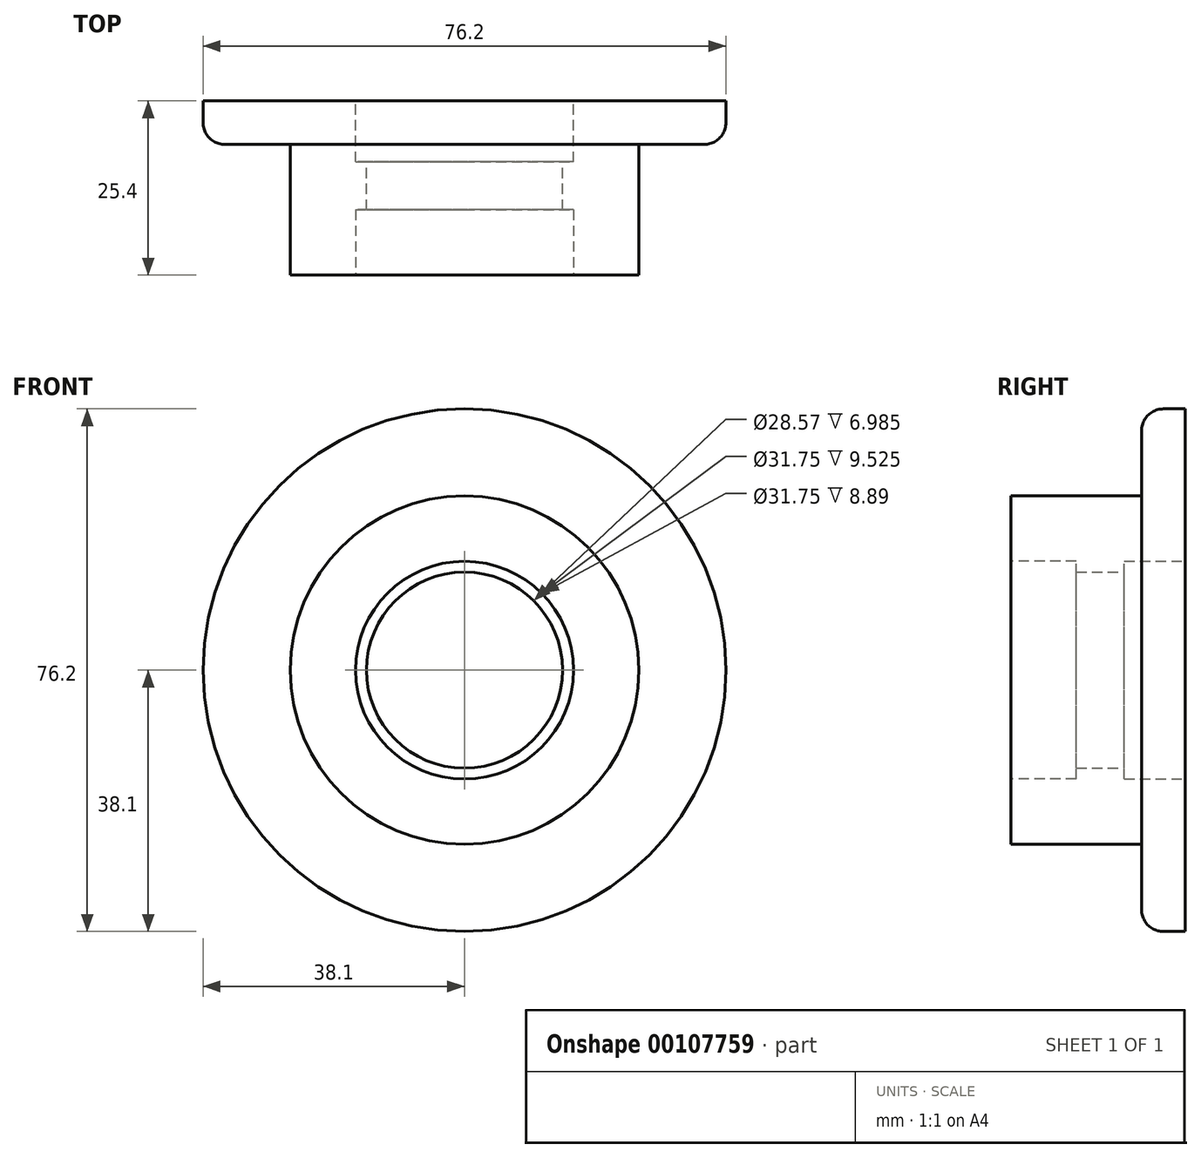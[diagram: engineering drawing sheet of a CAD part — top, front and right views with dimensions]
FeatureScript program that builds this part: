
annotation { "Feature Type Name" : "Feature", "Feature Type Description" : "" }
export const myFeature = defineFeature(function(context is Context, id is Id, definition is map)
    precondition{}
    {
        {
            var Q0;
            Q0=qCreatedBy(makeId("Front.planeOp"),FACE);
            var sketch = newSketch(context, id + "F0", { "sketchPlane" : qUnion([Q0])});
            skCircle(sketch, "E0", {"center": v(0, 0) * mm, "radius": 38.1 * mm});
            skSolve(sketch);
        }
        {
            var Q0;
            Q0=makeQuery(id+"F0.imprint","IMPRINT",FACE,{"disambiguationData":[TD([[makeQuery(id+"F0.imprint","IMPRINT",EDGE,{"derivedFrom":sQuery(id+"F0.wireOp",EDGE,"E0")}),1.0]])]});
            extrude(context, id + "F1", {"entities" : qUnion([Q0]), "depth" : 6.35 * mm});
        }
        {
            var Q0;
            Q0=makeQuery(id+"F1.opExtrude","CAP_FACE",FACE,{"disambiguationData":[OSD([sQuery(id+"F0.wireOp",EDGE,"E0")])],"isStart":false});
            var sketch = newSketch(context, id + "F2", { "sketchPlane" : qUnion([Q0])});
            skCircle(sketch, "E1", {"center": v(0, 0) * mm, "radius": 25.4 * mm});
            skSolve(sketch);
        }
        {
            var Q0;
            Q0=makeQuery(id+"F2.imprint","IMPRINT",FACE,{"disambiguationData":[TD([[makeQuery(id+"F2.imprint","IMPRINT",EDGE,{"derivedFrom":sQuery(id+"F2.wireOp",EDGE,"E1")}),1.0]])]});
            extrude(context, id + "F3", {"entities" : qUnion([Q0]), "operationType" : NewBodyOperationType.ADD, "depth" : 19.05 * mm});
        }
        {
            var Q0;
            Q0=qCreatedBy(makeId("Front.planeOp"),FACE);
            var sketch = newSketch(context, id + "F4", { "sketchPlane" : qUnion([Q0])});
            skCircle(sketch, "E2", {"center": v(0, 0) * mm, "radius": 15.88 * mm});
            skSolve(sketch);
        }
        {
            var Q0;
            Q0=sQuery(id+"F4.wireOp",VERTEX,"E2.center");
            var Q1;
            Q1=makeQuery(id+"F1.opExtrude","SWEPT_BODY",BODY,{"disambiguationData":[OSD([sQuery(id+"F0.wireOp",EDGE,"E0")])]});
            hole(context, id + "F5", {"style" : HoleStyle.SIMPLE, "endStyle" : HoleEndStyle.THROUGH, "oppositeDirection" : true, "holeDiameter" : 28.57 * mm, "startFromSketch" : true, "locations" : qUnion([Q0]), "scope" : qUnion([Q1]), "isTappedThrough" : true});
        }
        {
            var Q0;
            Q0=makeQuery(id+"F3.opExtrude","CAP_FACE",FACE,{"disambiguationData":[OSD([sQuery(id+"F2.wireOp",EDGE,"E1")])],"isStart":false});
            var sketch = newSketch(context, id + "F6", { "sketchPlane" : qUnion([Q0])});
            skCircle(sketch, "E3", {"center": v(0, 0) * mm, "radius": 15.88 * mm});
            skSolve(sketch);
        }
        {
            var Q0;
            Q0 = qSketchRegion(id + "F6", true);
            extrude(context, id + "F7", {"entities" : qUnion([Q0]), "operationType" : NewBodyOperationType.REMOVE, "oppositeDirection" : true, "depth" : 9.52 * mm});
        }
        {
            var Q0;
            Q0=makeQuery(id+"F1.opExtrude","CAP_EDGE",EDGE,{"disambiguationData":[OSD([sQuery(id+"F0.wireOp",EDGE,"E0")])],"isStart":false});
            fillet(context, id + "F8", {"entities" : qUnion([Q0]), "radius" : 3.17 * mm, "tangentPropagation" : true, "allowEdgeOverflow" : false});
        }
        {
            var Q0;
            Q0 = qSketchRegion(id + "F4", true);
            extrude(context, id + "F9", {"entities" : qUnion([Q0]), "operationType" : NewBodyOperationType.REMOVE, "depth" : 8.9 * mm});
        }
    });
